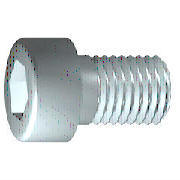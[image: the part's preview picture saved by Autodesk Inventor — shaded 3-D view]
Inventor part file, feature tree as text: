
AUTODESK INVENTOR PART (.ipt)
format: ipt  version: 2013 (Build 170138000, 138)  size: 183,296 bytes
history: native  units: mm (DEFAULTED — no unit token found)
features: sketch x2, extrude x1, plane x1, fillet x1
ambient origin geometry x7: Origin, YZ Plane, XY Plane, X Axis, Y Axis, Z Axis, Center Point
bodies: Solid1 (feature_tree), Body (feature_tree)
feature tree (5):
  extrude  "Slot"  Depth=0.306825mm
  plane  "Work Plane1"
  fillet  "Fillet2"  Radius=3.0mm
  sketch  "Sketch1"  dims[d1=18.0mm d2=0.306825mm d3=3.0mm]
  sketch  "Sketch2"  dims[d4=1.5mm d5=60.0deg d6=3.0mm d7=3.0mm d8=2.886751mm d9=5.5mm d10=90.0deg d11=10.0mm d12=0.0mm d13=18.0mm d14=0.0mm d15=0.306725mm d16=0.306725mm d17=0.3mm d19=0.0mm d26=25.0mm d27=45.0deg d28=0.0mm d29=0.0mm d30=0.1mm]
